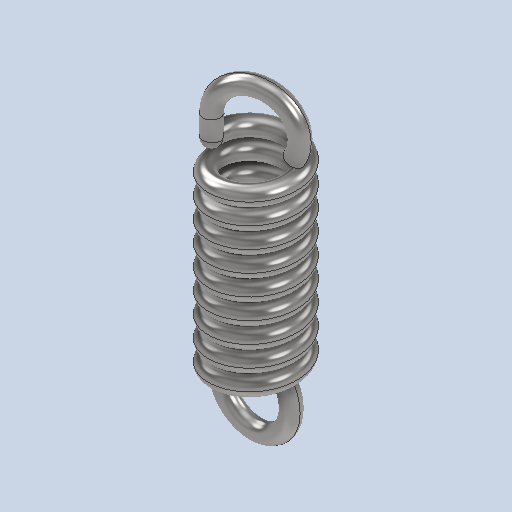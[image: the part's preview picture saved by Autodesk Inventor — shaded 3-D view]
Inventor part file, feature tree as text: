
AUTODESK INVENTOR PART (.ipt)
format: ipt  version: 2025 (Build 290162010, 162A)  size: 1,229,824 bytes
history: native  units: mm
features: sketch x97, plane x32, other x32, sweep x22, extrude x10, helix x4
ambient origin geometry x8: Origin, YZ Plane, XZ Plane, XY Plane, X Axis, Y Axis, Z Axis, Center Point
bodies: Solid1 (feature_tree)
feature tree (197):
  sketch  "3D Sketch2"
  plane  "ArbeitsebeneSweeping1"
  sweep  "Sweep1"
  other  "Erste Umdrehung mit Ösentyp 0(Rechts)"
  sketch  "Sketch8"  dims[d5=0.0mm d6=90.0deg d7=90.0deg d8=0.0mm d9=0.0mm d12=3.6mm]
  plane  "ArbeitsebeneExtrusion7"
  sketch  "Sketch10"  dims[d17=90.0deg d24=0.0mm d25=4.177895mm]
  plane  "ArbeitsebeneSweeping2"
  sweep  "Sweep2"
  other  "Zweite Umdrehung mit Ösentyp 0(Rechts)"
  sketch  "Sketch12"  dims[d26=10.0mm d27=90.476191mm]
  plane  "ArbeitsebeneExtrusion8"
  sketch  "Sketch110"  dims[d396=50.0mm]
  sketch  "3D Sketch20"
  plane  "ArbeitsebeneSweeping3"
  sweep  "Sweep3"
  sketch  "3D Sketch3"
  plane  "ArbeitsebeneSweeping6"
  sweep  "Sweep6"
  other  "Erste Umdrehung mit Ösentyp 0(Links)"
  sketch  "Sketch24"  dims[d171=0.0mm d172=90.0deg]
  plane  "ArbeitsebeneExtrusion5"
  sketch  "Sketch18"  dims[d86=90.0deg d87=20.0mm d90=20.0mm]
  plane  "ArbeitsebeneSweeping7"
  sweep  "Sweep7"
  other  "Zweite Umdrehung mit Ösentyp 0(Links)"
  sketch  "Sketch20"  dims[d149=90.0deg d152=20.0mm]
  plane  "ArbeitsebeneExtrusion6"
  sketch  "Sketch22"  dims[d169=300.0deg d170=4.775mm]
  plane  "ArbeitsebeneSweeping8"
  sweep  "Sweep8"
  other  "Erste Umdrehung mit Ösentyp 1(Links)"
  sketch  "Sketch27"  dims[d175=0.0mm d176=300.0deg]
  plane  "ArbeitsebeneExtrusion9"
  extrude  "Extrusion9"  Depth=10.0mm
  sketch  "Sketch29"  dims[d179=30.0mm d180=90.0deg]
  plane  "ArbeitsebeneSweeping9"
  sweep  "Sweep9"
  other  "Zweite Umdrehung mit Ösentyp 1(Links)"
  sketch  "Sketch32"  dims[d183=0.0mm d184=30.0mm d185=30.0mm d186=30.0mm]
  plane  "ArbeitsebeneExtrusion10"
  sketch  "Sketch34"  dims[d189=7.2mm d190=0.0mm]
  sketch  "3D Sketch22"
  plane  "ArbeitsebeneSweeping10"
  sweep  "Sweep10"
  other  "Erste Umdrehung mit Ösentyp 1(Rechts)"
  sketch  "Sketch42"  dims[d195=40.0mm d196=7.2mm]
  plane  "ArbeitsebeneExtrusion11"
  extrude  "Extrusion11"  Depth=20.0mm
  sketch  "Sketch44"  dims[d199=300.0deg d200=4.775mm]
  plane  "ArbeitsebeneSweeping11"
  sweep  "Sweep11"
  other  "Zweite Umdrehung mit Ösentyp 1(Rechts)"
  sketch  "Sketch112"  dims[d397=29.670597mm]
  plane  "ArbeitsebeneExtrusion12"
  sketch  "Sketch114"  dims[d401=50.0mm]
  sketch  "3D Sketch24"
  plane  "ArbeitsebeneSweeping12"
  sweep  "Sweep12"
  sketch  "Sketch46"  dims[d201=0.0mm d202=90.0deg]
  other  "Erstes Sweeping mit Ösentyp 2(Links)"
  sweep  "SweepingLinksÖse21"
  sketch  "Sketch48"  dims[d206=300.0deg d207=4.775mm]
  other  "Zweites Sweeping mit Ösentyp 2(Links)"
  sweep  "SweepingLinksÖse22"
  sketch  "Sketch50"  dims[d210=7.2mm d211=0.0mm d212=90.0deg d213=300.0deg d214=4.775mm]
  other  "Erstes Sweeping mit Ösentyp 2(Rechts)"
  sweep  "SweepingRechtsÖse21"
  sketch  "Sketch52"  dims[d220=50.0mm]
  other  "Zweites Sweeping mit Ösentyp 2(Rechts)"
  sweep  "SweepingRechtsÖse22"
  other  "Erste Umdrehung mit Ösentyp 3(Links)"
  extrude  "Extrusion1"  TaperAngle=90.0deg  [1 undecoded]
  sweep  "Sweep19"
  other  "Zweite Umdrehung mit Ösentyp 3(Links)"
  extrude  "Extrusion2"  Depth=30.0mm
  sketch  "Sketch60"  dims[d242=90.0deg]
  plane  "ArbeitsebeneSweeping20"
  sweep  "Sweep20"
  other  "Erste Umdrehung mit Ösentyp 3(Rechts)"
  extrude  "Extrusion3"  TaperAngle=0.0deg  [1 undecoded]
  sweep  "Sweep21"
  other  "Zweite Umdrehung mit Ösentyp 3(Rechts)"
  extrude  "Extrusion4"  TaperAngle=90.0deg  [1 undecoded]
  sketch  "Sketch68"  dims[d282=60.0mm]
  plane  "Work Plane46"
  sweep  "Sweep22"
  other  "Erste Umdrehung mit Ösentyp 4(Links)"
  sketch  "Sketch71"  dims[d301=10.0mm d302=15.0mm d303=0.0mm d304=90.0deg d305=90.0deg d306=0.0mm d307=0.0mm]
  plane  "ArbeitsebeneExtrusion13"
  extrude  "Extrusion13"  TaperAngle=90.0deg  [1 undecoded]
  sketch  "Sketch73"  dims[d310=4.1mm]
  plane  "ArbeitsebeneSweeping23"
  sweep  "Sweep23"
  other  "Zweite Umdrehung mit Ösentyp 4(Links)"
  sketch  "Sketch76"  dims[d320=5.675mm]
  plane  "ArbeitsebeneExtrusion14"
  sketch  "Sketch78"  dims[d322=10.0mm d323=15.0mm d324=0.0mm d325=90.0deg d326=90.0deg d327=0.0mm d328=0.0mm d329=70.0mm]
  sketch  "3D Sketch26"
  plane  "ArbeitsebeneSweeping24"
  sweep  "Sweep24"
  other  "Erste Umdrehung mit Ösentyp 4(Rechts)"
  sketch  "Sketch86"  dims[d332=10.0mm d333=15.0mm d334=0.0mm d335=90.0deg d336=90.0deg d337=0.0mm d338=0.0mm d339=70.0mm]
  plane  "Work PlaneExtrusion15"
  extrude  "Extrusion15"  Depth=7.2mm TaperAngle=0.0deg
  sketch  "Sketch88"  dims[d361=10.0mm]
  plane  "ArbeitsebeneSweeping25"
  sweep  "Sweep25"
  other  "Zweite Umdrehung mit Ösentyp 4(Rechts)"
  sketch  "Sketch116"  dims[d404=4.15mm]
  plane  "ArbeitsebeneExtrusion16"
  sketch  "Sketch118"  dims[d406=50.0mm d407=29.670597mm d408=0.0mm d411=60.0mm d423=60.0mm d433=4.15mm d434=0.0mm d435=4.775mm d436=4.1mm d437=10.0mm d438=15.0mm d439=0.0mm d440=90.0deg d441=90.0deg d442=0.0mm d443=0.0mm d444=60.0mm d447=60.0mm d457=4.15mm d458=0.0mm d459=60.0mm d469=90.0deg d478=90.0deg d479=4.775mm d480=4.1mm d481=25.4mm d482=15.0mm d483=0.0mm d484=90.0deg d485=90.0deg d486=0.0mm d487=0.0mm d491=10.0mm d498=10.0mm d501=0.0mm d502=4.15mm d503=0.0mm d504=210.0deg d505=0.0mm d506=0.0mm d507=4.15mm d508=0.0mm d509=29.670597mm d510=0.0mm d511=10.0mm d512=0.0mm d513=4.15mm d514=0.0mm d515=29.670597mm d516=0.0mm d517=0.0mm d518=4.15mm d519=0.0mm d520=4.775mm d521=4.1mm d522=10.0mm d523=15.0mm d524=0.0mm d525=90.0deg d526=90.0deg d527=0.0mm d528=0.0mm d529=60.0mm d530=50.0mm d531=0.0mm d532=4.15mm d533=0.0mm d534=20.0mm d535=210.0deg d536=0.0mm d537=0.0mm d538=4.15mm d539=0.0mm d540=29.670597mm d541=0.0mm d542=50.0mm d543=0.0mm d544=4.15mm d545=0.0mm d546=60.0mm d547=4.775mm d548=4.1mm d549=10.0mm d550=15.0mm d551=0.0mm d552=90.0deg d553=90.0deg d554=0.0mm d555=0.0mm d561=10.0mm d564=0.0mm d565=4.15mm d566=0.0mm d567=10.0mm d569=29.670597mm d570=0.0mm d571=90.0deg d578=0.0mm d579=3.6mm d580=4.15mm d581=0.0mm d584=10.0mm d585=10.0mm d588=29.670597mm d589=0.0mm d590=0.0mm d591=0.0mm d592=0.0mm d593=0.0mm d594=0.0mm d595=0.0mm d596=0.0mm d597=0.0mm d598=0.0mm d599=0.0mm d600=0.0mm d601=0.0mm d602=0.0mm d603=0.0mm d604=0.0mm d605=0.0mm d606=0.0mm d607=0.0mm d608=0.0mm d609=0.0mm d610=0.0mm d611=0.0mm]
  sketch  "3D Sketch28"
  plane  "ArbeitsebeneSweeping26"
  sweep  "Sweep26"
  other  "Erste Umdrehung mit Ösentyp 5(Links)"
  sketch  "Sketch91"  dims[d365=0.0mm]
  plane  "ArbeitsebeneExtrusion17"
  extrude  "Extrusion17"  TaperAngle=0.0deg  [1 undecoded]
  helix  "Coil1"  [1 undecoded]
  other  "Zweite Umdrehung mit Ösentyp 5(Links)"
  sketch  "Sketch95"  dims[d373=20.0mm]
  plane  "ArbeitsebeneExtrusion18"
  helix  "Coil2"  [1 undecoded]
  other  "Erste Umdrehung mit Ösentyp 5(Rechts)"
  sketch  "Sketch99"  dims[d377=210.0deg]
  plane  "ArbeitsebeneExtrusion19"
  helix  "Coil13"  [1 undecoded]
  other  "Zweite Umdrehung mit Ösentyp 5(Rechts)"
  sketch  "Sketch103"  dims[d385=0.0mm]
  plane  "ArbeitsebeneExtrusion20"
  extrude  "Extrusion20"  Depth=40.0mm
  sketch  "Sketch105"  dims[d387=210.0deg]
  helix  "Coil4"  [1 undecoded]
  other  "Erste Spirale mit Ösentyp 6(Links)"
  other  "Zweite Spirale mit Ösentyp 6(Links)"
  other  "Erste Spirale mit Ösentyp 6(Rechts)"
  other  "Zweite Spirale mit Ösentyp 6(Rechts)"
  other  "Srf1"
  sketch  "Sketch4"  dims[d0=0.9mm d1=7.2mm]
  sketch  "Sketch7"  dims[d2=4.177895mm d3=10.0mm d4=90.476191mm]
  other  "Srf2"
  sketch  "Sketch16"  dims[d38=90.0deg d54=10.0mm d55=10.0mm]
  sketch  "Sketch26"  dims[d173=300.0deg d174=4.775mm]
  sketch  "Sketch31"  dims[d181=300.0deg d182=5.675mm]
  sketch  "Sketch36"  dims[d191=300.0deg d192=4.775mm]
  sketch  "Sketch41"  dims[d193=0.0mm d194=90.0deg]
  sketch  "Sketch47"  dims[d203=40.0mm d204=7.2mm d205=0.0mm]
  sketch  "Sketch49"  dims[d208=0.0mm d209=90.0deg]
  sketch  "Sketch51"  dims[d215=0.0mm d216=40.0mm d217=90.0deg]
  sketch  "Sketch53"  dims[d223=90.0deg]
  sketch  "Sketch54"  dims[d226=50.0mm]
  sketch  "Sketch55"  dims[d229=90.0deg]
  sketch  "Sketch56"  dims[d232=50.0mm]
  sketch  "Sketch58"  dims[d235=90.0deg]
  sketch  "Sketch59"  dims[d238=50.0mm]
  sketch  "Sketch61"  dims[d243=60.0mm]
  sketch  "Sketch62"  dims[d255=90.0deg]
  sketch  "Sketch63"  dims[d256=60.0mm]
  sketch  "Sketch64"  dims[d268=90.0deg]
  sketch  "Sketch66"  dims[d269=60.0mm]
  sketch  "Sketch67"  dims[d281=90.0deg]
  sketch  "Sketch69"  dims[d299=5.675mm]
  sketch  "Sketch70"  dims[d300=4.1mm]
  sketch  "Sketch75"  dims[d311=10.0mm d312=15.0mm d313=0.0mm d314=90.0deg d315=90.0deg d316=0.0mm d317=0.0mm d318=70.0mm d319=70.0mm]
  sketch  "Sketch80"  dims[d330=5.675mm]
  sketch  "Sketch85"  dims[d331=4.1mm]
  sketch  "Sketch90"  dims[d364=4.15mm]
  sketch  "Sketch94"  dims[d368=0.0mm]
  sketch  "Sketch98"  dims[d376=20.0mm]
  sketch  "Sketch102"  dims[d384=4.15mm]
  sketch  "Sketch106"  dims[d388=0.0mm]
  sketch  "Sketch107"  dims[d391=50.0mm]
  sketch  "Sketch108"  dims[d394=4.15mm]
  sketch  "Sketch109"  dims[d395=0.0mm]
  sketch  "Sketch13"  dims[d28=0.0mm d29=90.0deg d30=90.0deg d31=0.0mm d32=0.0mm d33=3.6mm]
  sketch  "Sketch33"  dims[d187=90.0deg d188=40.0mm]
  sketch  "Sketch113"  dims[d398=0.0mm]
  sketch  "Sketch77"  dims[d321=4.1mm]
  sketch  "Sketch117"  dims[d405=0.0mm]
  sketch  "Sketch96"  dims[d374=4.15mm]
  sketch  "Sketch97"  dims[d375=0.0mm]
  sketch  "Sketch104"  dims[d386=20.0mm]
  sketch  "Sketch43"  dims[d197=0.0mm d198=90.0deg]
  sketch  "Sketch9"  dims[d13=0.0mm d14=90.0deg]
  sketch  "Sketch87"  dims[d350=10.0mm d352=10.0mm d353=10.0mm d356=10.0mm]
  sketch  "Sketch100"  dims[d378=0.0mm]
  sketch  "Sketch101"  dims[d381=20.0mm]
  sketch  "Sketch28"  dims[d177=5.675mm d178=0.0mm]
  sketch  "Sketch72"  dims[d308=5.675mm]
  sketch  "Sketch92"  dims[d366=10.0mm]
  sketch  "Sketch93"  dims[d367=29.670597mm]
  sketch  "Sketch21"  dims[d155=90.0deg d156=20.0mm]
  sketch  "Sketch15"  dims[d34=0.0mm d36=0.0mm]
  sketch  "Sketch17"  dims[d72=0.0mm d73=0.0mm d79=90.0deg]
  other  "Basisschraube(Rechts)"
  other  "Basisschraube(Links)"
note: 9 required parameter values undecoded (feature->parameter linkage not recoverable at this tier; creation-order binding heuristic only, values carry confidence <= 0.55)
